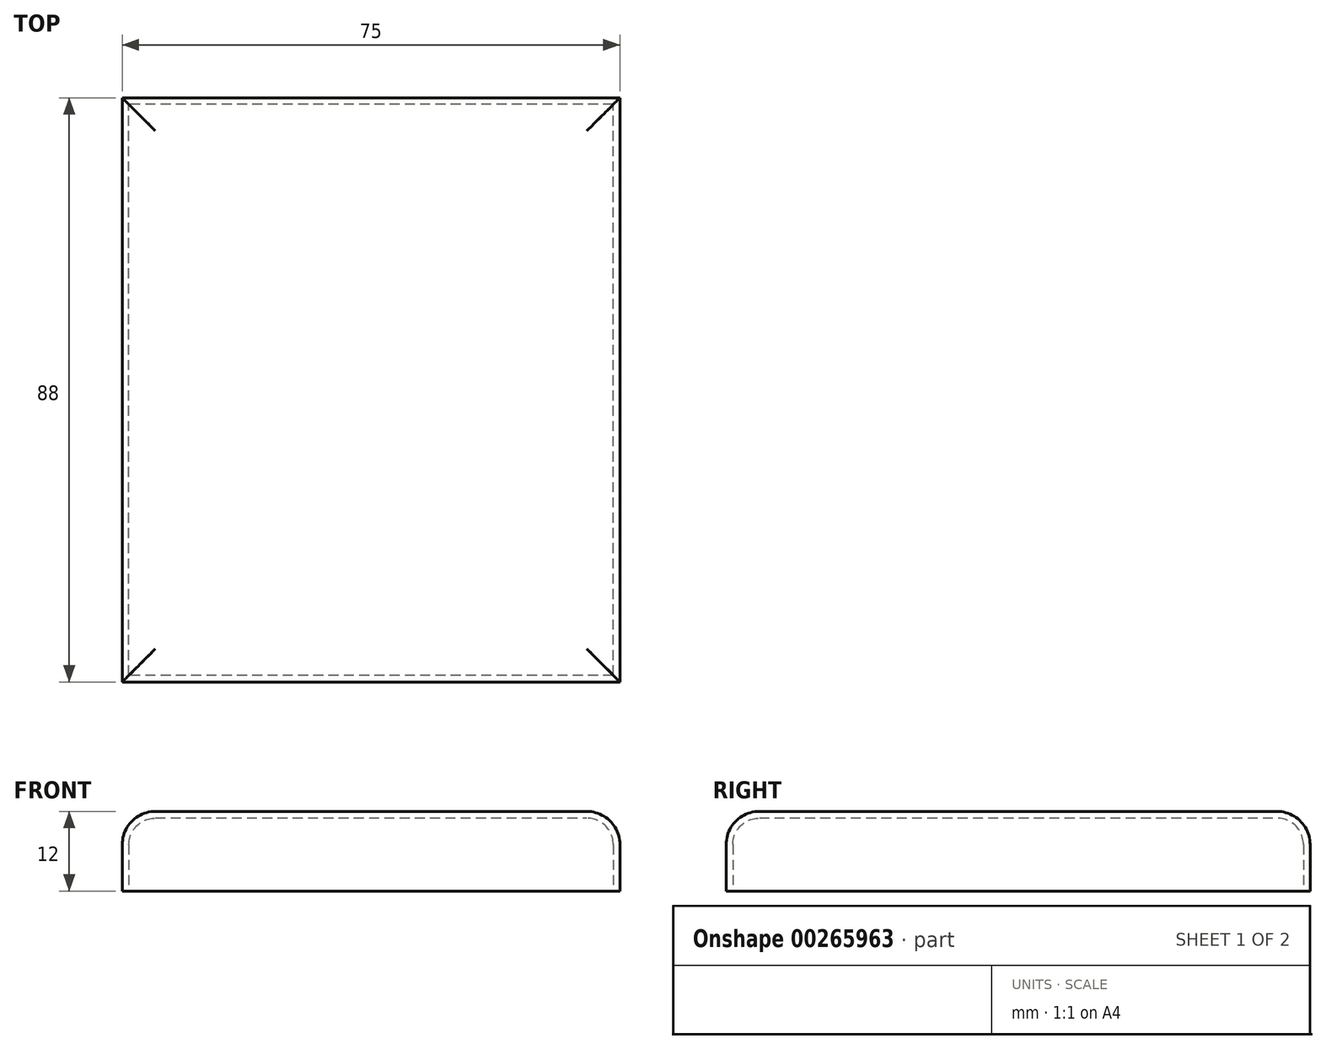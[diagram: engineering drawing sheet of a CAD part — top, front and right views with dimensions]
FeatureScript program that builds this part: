
annotation { "Feature Type Name" : "Feature", "Feature Type Description" : "" }
export const myFeature = defineFeature(function(context is Context, id is Id, definition is map)
    precondition{}
    {
        {
            var Q0;
            Q0=qCreatedBy(makeId("Top.planeOp"),FACE);
            var sketch = newSketch(context, id + "F0", { "sketchPlane" : qUnion([Q0])});
            skLineSegment(sketch, "E0.bottom", {"start": v(37.5, -44) * mm, "end": v(-37.5, -44) * mm});
            skLineSegment(sketch, "E0.top", {"start": v(37.5, 44) * mm, "end": v(-37.5, 44) * mm});
            skLineSegment(sketch, "E0.left", {"start": v(37.5, -44) * mm, "end": v(37.5, 44) * mm});
            skLineSegment(sketch, "E0.right", {"start": v(-37.5, -44) * mm, "end": v(-37.5, 44) * mm});
            skPoint(sketch, "E0.middle", {"position": v(0, 0) * mm});
            skSolve(sketch);
        }
        {
            var Q0;
            Q0 = qSketchRegion(id + "F0", true);
            extrude(context, id + "F1", {"entities" : qUnion([Q0]), "depth" : 12 * mm});
        }
        {
            var Q0;
            Q0=makeQuery(id+"F1.opExtrude","CAP_FACE",FACE,{"disambiguationData":[OSD([sQuery(id+"F0.wireOp",EDGE,"E0.bottom"),sQuery(id+"F0.wireOp",EDGE,"E0.top"),sQuery(id+"F0.wireOp",EDGE,"E0.left"),sQuery(id+"F0.wireOp",EDGE,"E0.right")])],"isStart":false});
            fillet(context, id + "F2", {"entities" : qUnion([Q0]), "radius" : 5 * mm, "tangentPropagation" : true, "allowEdgeOverflow" : false});
        }
        {
            var Q0;
            Q0=makeQuery(id+"F1.opExtrude","CAP_FACE",FACE,{"disambiguationData":[OSD([sQuery(id+"F0.wireOp",EDGE,"E0.bottom"),sQuery(id+"F0.wireOp",EDGE,"E0.top"),sQuery(id+"F0.wireOp",EDGE,"E0.left"),sQuery(id+"F0.wireOp",EDGE,"E0.right")])],"isStart":true});
            shell(context, id + "F3", {"entities" : qUnion([Q0]), "thickness" : 1 * mm});
        }
    });
